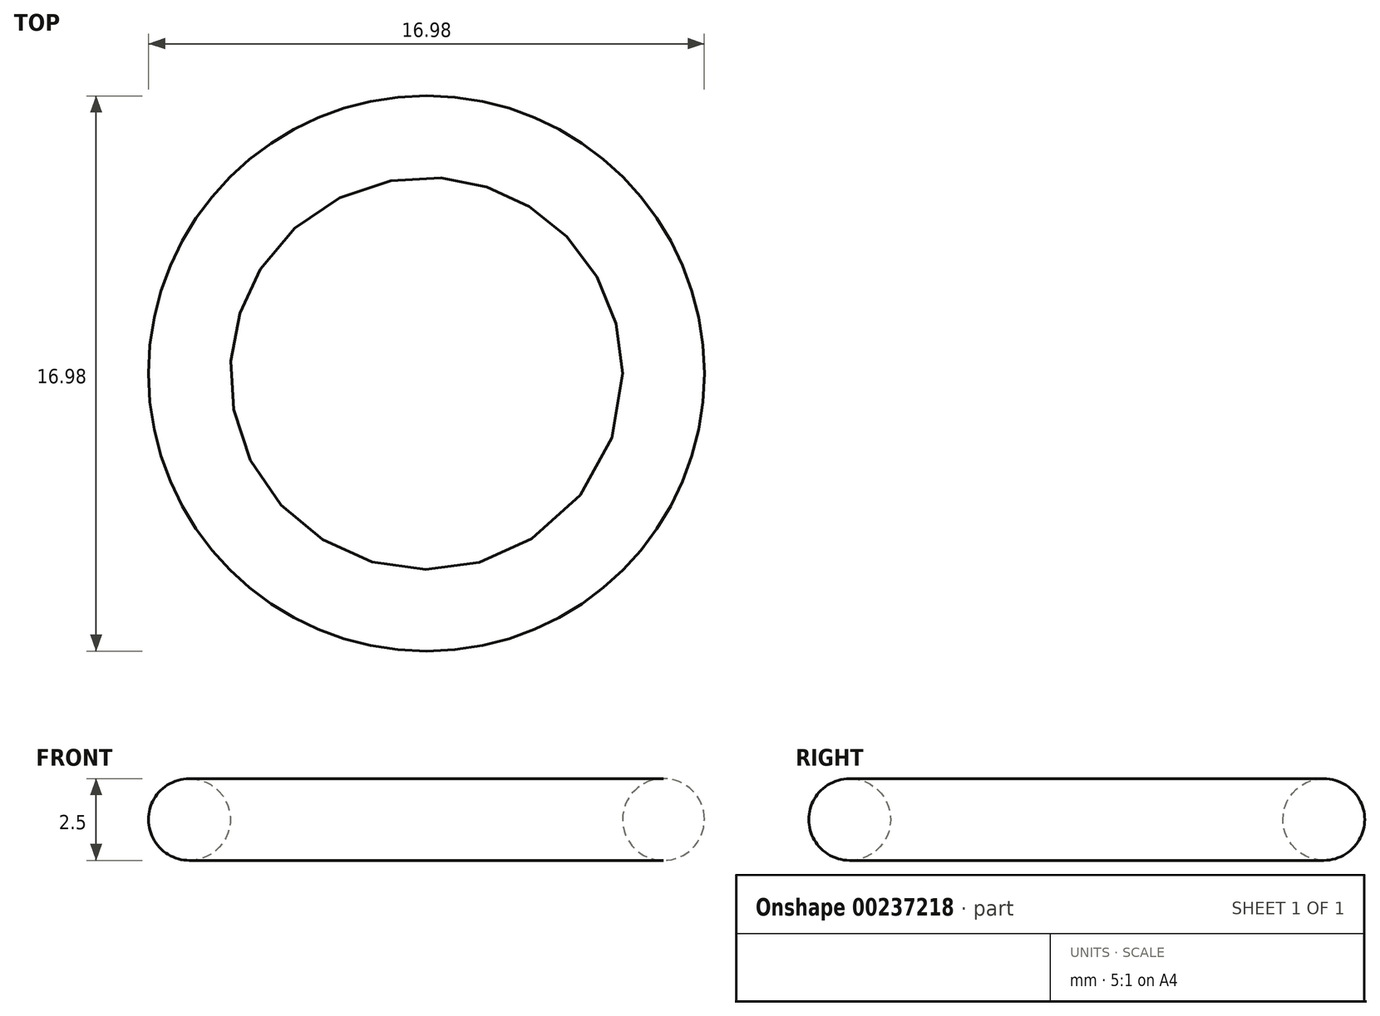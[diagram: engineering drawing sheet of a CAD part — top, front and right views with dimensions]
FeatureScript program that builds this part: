
annotation { "Feature Type Name" : "Feature", "Feature Type Description" : "" }
export const myFeature = defineFeature(function(context is Context, id is Id, definition is map)
    precondition{}
    {
        {
            var Q0;
            Q0=qCreatedBy(makeId("Top.planeOp"),FACE);
            var sketch = newSketch(context, id + "F0", { "sketchPlane" : qUnion([Q0])});
            skCircle(sketch, "E0", {"center": v(0, 0) * mm, "radius": 7.25 * mm});
            skCircle(sketch, "E1", {"center": v(0, 0) * mm, "radius": 6 * mm});
            skCircle(sketch, "E2", {"center": v(0, 0) * mm, "radius": 8.5 * mm});
            skSolve(sketch);
        }
        {
            var Q0;
            Q0=qCreatedBy(makeId("Right.planeOp"),FACE);
            var sketch = newSketch(context, id + "F1", { "sketchPlane" : qUnion([Q0])});
            skCircle(sketch, "E3", {"center": v(7.24, 0) * mm, "radius": 1.25 * mm});
            skSolve(sketch);
        }
        {
            var Q0;
            Q0=makeQuery(id+"F1.imprint","IMPRINT",FACE,{"disambiguationData":[TD([[makeQuery(id+"F1.imprint","IMPRINT",EDGE,{"derivedFrom":sQuery(id+"F1.wireOp",EDGE,"E3")}),1.0]])]});
            var Q1;
            Q1=sQuery(id+"F0.wireOp",EDGE,"E0");
            var Q2;
            Q2=sQuery(id+"F0.wireOp",EDGE,"E1");
            var Q3;
            Q3=sQuery(id+"F0.wireOp",EDGE,"E0");
            sweep(context, id + "F2", {"profiles" : qUnion([Q0]), "surfaceProfiles" : qUnion([Q1, Q2]), "path" : qUnion([Q3])});
        }
    });
